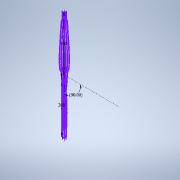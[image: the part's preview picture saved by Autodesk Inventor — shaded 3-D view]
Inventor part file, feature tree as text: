
AUTODESK INVENTOR PART (.ipt)
format: ipt  version: 2022 (Build 260153000, 153)  size: 1,730,048 bytes
history: native  units: mm
features: sketch x7, sweep x2
ambient origin geometry x8: Origin, YZ Plane, XZ Plane, XY Plane, X Axis, Y Axis, Z Axis, Center Point
bodies: Solid1 (feature_tree)
feature tree (9):
  sketch  "Sketch1"  dims[d1=0.0mm d2=380.0mm]
  sketch  "Sketch2"  dims[d5=0.0mm d6=0.0mm d7=330.0mm]
  sketch  "3D Sketch1"
  sweep  "Sweep1"
  sweep  "Sweep2"
  sketch  "Sketch5"  dims[d9=0.0mm d10=0.0mm d11=380.0mm d12=90.0deg]
  sketch  "3D Sketch3"
  sketch  "Sketch4"  dims[d8=90.0deg]
  sketch  "3D Sketch2"
